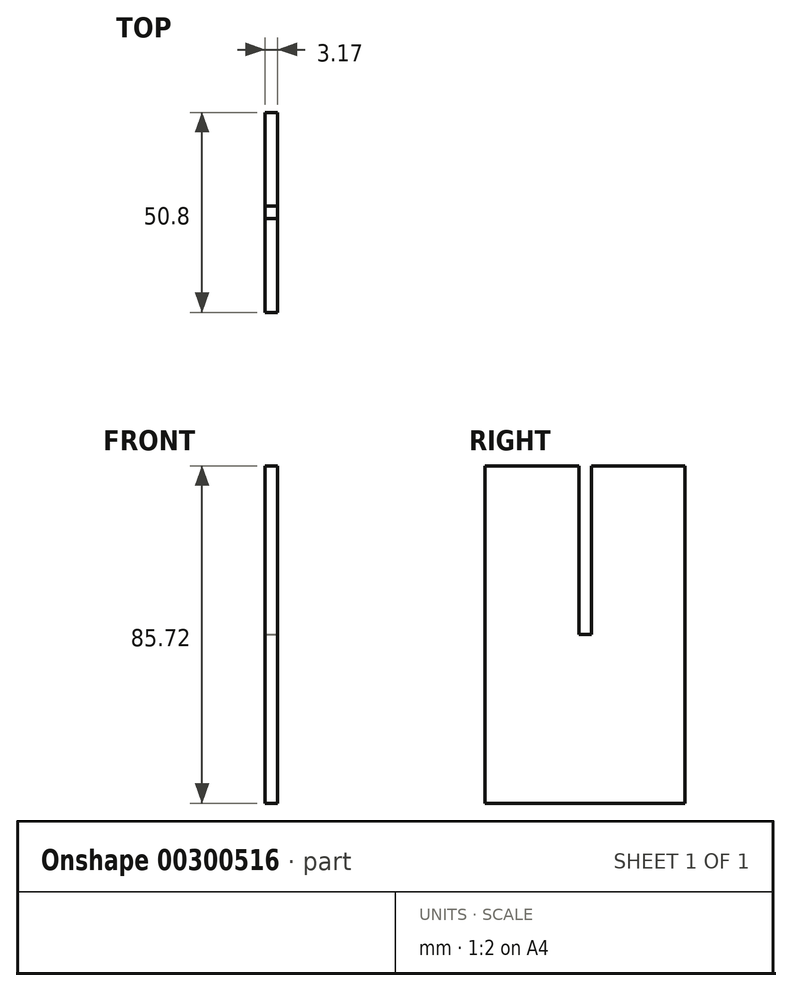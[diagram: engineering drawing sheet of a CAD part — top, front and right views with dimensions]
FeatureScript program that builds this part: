
annotation { "Feature Type Name" : "Feature", "Feature Type Description" : "" }
export const myFeature = defineFeature(function(context is Context, id is Id, definition is map)
    precondition{}
    {
        {
            var Q0;
            Q0=qCreatedBy(makeId("Right.planeOp"),FACE);
            var sketch = newSketch(context, id + "F0", { "sketchPlane" : qUnion([Q0])});
            skLineSegment(sketch, "E0.bottom", {"start": v(-25.4, 42.86) * mm, "end": v(25.4, 42.86) * mm});
            skLineSegment(sketch, "E0.top", {"start": v(-25.4, -42.86) * mm, "end": v(25.4, -42.86) * mm});
            skLineSegment(sketch, "E0.left", {"start": v(-25.4, 42.86) * mm, "end": v(-25.4, -42.86) * mm});
            skLineSegment(sketch, "E0.right", {"start": v(25.4, 42.86) * mm, "end": v(25.4, -42.86) * mm});
            skPoint(sketch, "E0.middle", {"position": v(0, 0) * mm});
            skSolve(sketch);
        }
        {
            var Q0;
            Q0 = qSketchRegion(id + "F0", true);
            extrude(context, id + "F1", {"entities" : qUnion([Q0]), "depth" : 3.17 * mm});
        }
        {
            var Q0;
            Q0=makeQuery(id+"F1.opExtrude","CAP_FACE",FACE,{"disambiguationData":[OSD([sQuery(id+"F0.wireOp",EDGE,"E0.bottom"),sQuery(id+"F0.wireOp",EDGE,"E0.top"),sQuery(id+"F0.wireOp",EDGE,"E0.left"),sQuery(id+"F0.wireOp",EDGE,"E0.right")])],"isStart":false});
            var sketch = newSketch(context, id + "F2", { "sketchPlane" : qUnion([Q0])});
            skLineSegment(sketch, "E1.bottom", {"start": v(-1.59, 42.86) * mm, "end": v(1.59, 42.86) * mm});
            skLineSegment(sketch, "E1.top", {"start": v(-1.59, 0) * mm, "end": v(1.59, 0) * mm});
            skLineSegment(sketch, "E1.left", {"start": v(-1.59, 42.86) * mm, "end": v(-1.59, 0) * mm});
            skLineSegment(sketch, "E1.right", {"start": v(1.59, 42.86) * mm, "end": v(1.59, 0) * mm});
            skSolve(sketch);
        }
        {
            var Q0;
            Q0 = qSketchRegion(id + "F2", true);
            extrude(context, id + "F3", {"entities" : qUnion([Q0]), "operationType" : NewBodyOperationType.REMOVE, "endBound" : BoundingType.THROUGH_ALL, "oppositeDirection" : true, "depth" : 25.4 * mm});
        }
    });
